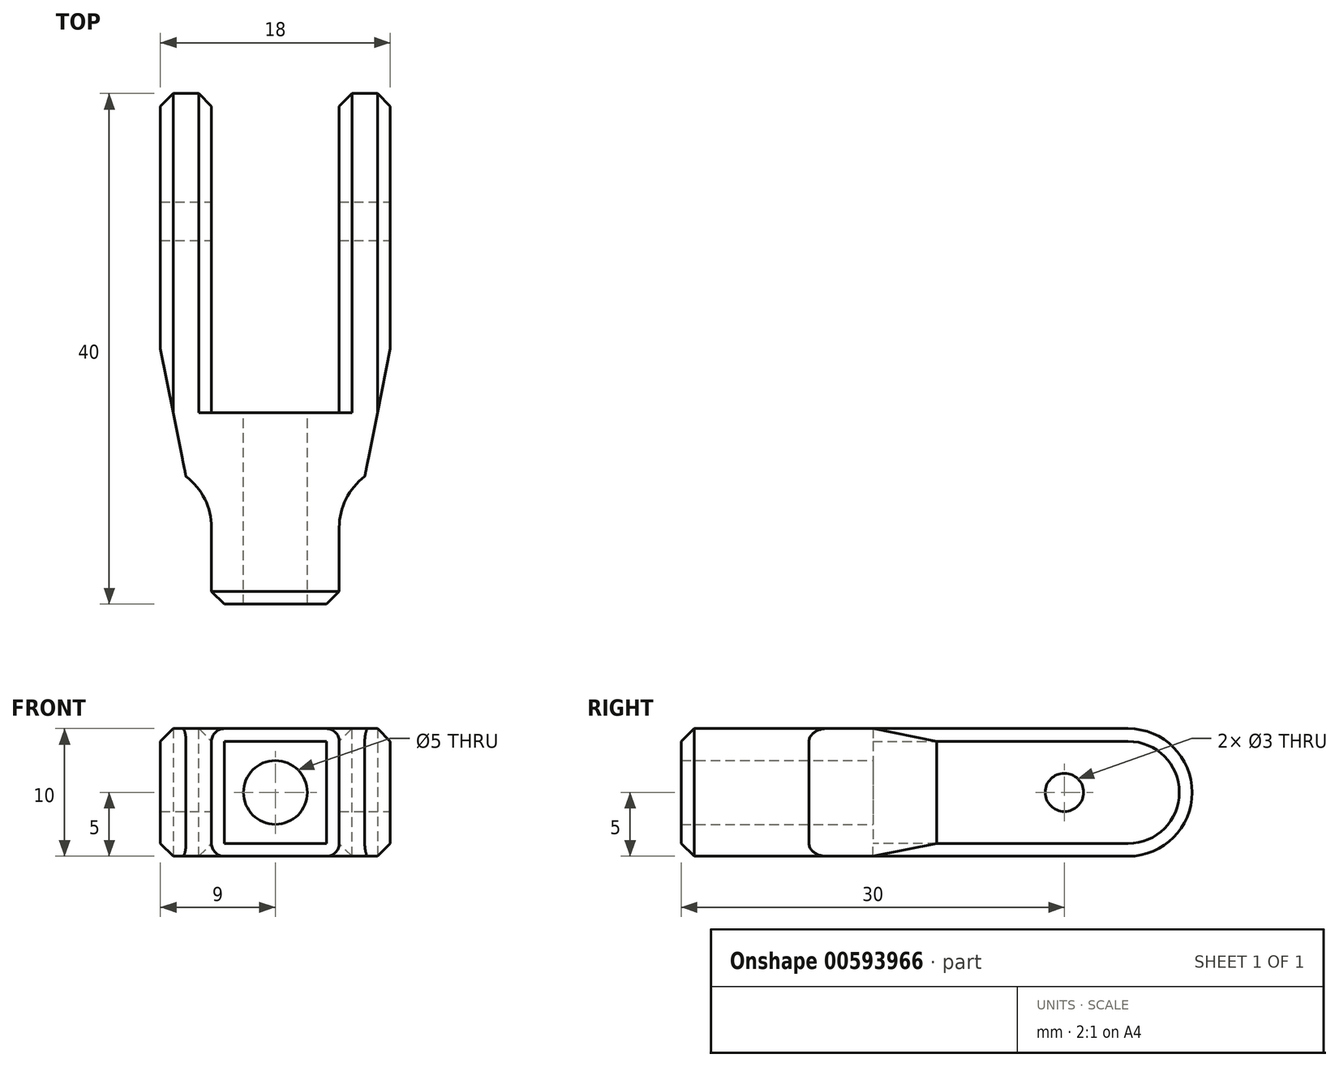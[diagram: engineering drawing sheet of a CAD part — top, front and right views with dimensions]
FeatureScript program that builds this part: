
annotation { "Feature Type Name" : "Feature", "Feature Type Description" : "" }
export const myFeature = defineFeature(function(context is Context, id is Id, definition is map)
    precondition{}
    {
        {
            var Q0;
            Q0=qCreatedBy(makeId("Top.planeOp"),FACE);
            var sketch = newSketch(context, id + "F0", { "sketchPlane" : qUnion([Q0])});
            skLineSegment(sketch, "E0.bottom", {"start": v(-5, 10) * mm, "end": v(5, 10) * mm});
            skLineSegment(sketch, "E0.top", {"start": v(-5, -10) * mm, "end": v(5, -10) * mm});
            skLineSegment(sketch, "E0.left", {"start": v(-5, 10) * mm, "end": v(-5, -10) * mm});
            skLineSegment(sketch, "E0.right", {"start": v(5, 10) * mm, "end": v(5, -10) * mm});
            skPoint(sketch, "E0.middle", {"position": v(0, 0) * mm});
            skLineSegment(sketch, "E1.bottom", {"start": v(-7, 20) * mm, "end": v(7, 20) * mm});
            skLineSegment(sketch, "E1.top", {"start": v(-7, 0) * mm, "end": v(7, 0) * mm});
            skLineSegment(sketch, "E1.left", {"start": v(-7, 20) * mm, "end": v(-7, 0) * mm});
            skLineSegment(sketch, "E1.right", {"start": v(7, 20) * mm, "end": v(7, 0) * mm});
            skPoint(sketch, "E1.middle", {"position": v(0, 10) * mm});
            skLineSegment(sketch, "E2.bottom", {"start": v(-5, 10) * mm, "end": v(-9, 10) * mm});
            skLineSegment(sketch, "E2.top", {"start": v(-5, 30) * mm, "end": v(-9, 30) * mm});
            skLineSegment(sketch, "E2.left", {"start": v(-5, 10) * mm, "end": v(-5, 30) * mm});
            skLineSegment(sketch, "E2.right", {"start": v(-9, 10) * mm, "end": v(-9, 30) * mm});
            skPoint(sketch, "E2.middle", {"position": v(-7, 20) * mm});
            skLineSegment(sketch, "E3.bottom", {"start": v(5, 10) * mm, "end": v(9, 10) * mm});
            skLineSegment(sketch, "E3.top", {"start": v(5, 30) * mm, "end": v(9, 30) * mm});
            skLineSegment(sketch, "E3.left", {"start": v(5, 10) * mm, "end": v(5, 30) * mm});
            skLineSegment(sketch, "E3.right", {"start": v(9, 10) * mm, "end": v(9, 30) * mm});
            skPoint(sketch, "E3.middle", {"position": v(7, 20) * mm});
            skLineSegment(sketch, "E4", {"start": v(-9, 10) * mm, "end": v(-7, 0) * mm});
            skLineSegment(sketch, "E5", {"start": v(7, 0) * mm, "end": v(9, 10) * mm});
            skCircle(sketch, "E6", {"center": v(0, 10) * mm, "radius": 5 * mm});
            skPoint(sketch, "E7", {"position": v(0, 5) * mm});
            skLineSegment(sketch, "E8", {"start": v(-5, 5) * mm, "end": v(5, 5) * mm});
            skSolve(sketch);
        }
        {
            var Q0;
            {var subQ0=sQuery(id+"F0.wireOp",EDGE,"E0.top");Q0=makeQuery(id+"F0.imprint","IMPRINT",FACE,{"disambiguationData":[TD([[makeQuery(id+"F0.imprint","IMPRINT",EDGE,{"derivedFrom":subQ0}),1.0]])]});}
            var Q1;
            {var subQ1=sQuery(id+"F0.wireOp",EDGE,"E0.right");var subQ3=sQuery(id+"F0.wireOp",EDGE,"E1.top");var subQ4=makeQuery(id+"F0.imprint","INTERSECT",VERTEX,{"derivedFrom":[subQ1,subQ3]});Q1=makeQuery(id+"F0.imprint","IMPRINT",FACE,{"disambiguationData":[TD([[makeQuery(id+"F0.imprint","IMPRINT",EDGE,{"disambiguationData":[TD([[subQ4,-1.0]])],"derivedFrom":subQ3}),1.0]])]});}
            var Q2;
            {var subQ0=sQuery(id+"F0.wireOp",EDGE,"E5");Q2=makeQuery(id+"F0.imprint","IMPRINT",FACE,{"disambiguationData":[TD([[makeQuery(id+"F0.imprint","IMPRINT",EDGE,{"derivedFrom":subQ0}),1.0]])]});}
            var Q3;
            {var subQ0=sQuery(id+"F0.wireOp",EDGE,"E3.top");Q3=makeQuery(id+"F0.imprint","IMPRINT",FACE,{"disambiguationData":[TD([[makeQuery(id+"F0.imprint","IMPRINT",EDGE,{"derivedFrom":subQ0}),-1.0]])]});}
            var Q4;
            {var subQ1=sQuery(id+"F0.wireOp",EDGE,"E0.left");var subQ3=sQuery(id+"F0.wireOp",EDGE,"E1.top");var subQ4=makeQuery(id+"F0.imprint","INTERSECT",VERTEX,{"derivedFrom":[subQ1,subQ3]});Q4=makeQuery(id+"F0.imprint","IMPRINT",FACE,{"disambiguationData":[TD([[makeQuery(id+"F0.imprint","IMPRINT",EDGE,{"disambiguationData":[TD([[subQ4,1.0]])],"derivedFrom":subQ3}),1.0]])]});}
            var Q5;
            {var subQ0=sQuery(id+"F0.wireOp",EDGE,"E4");Q5=makeQuery(id+"F0.imprint","IMPRINT",FACE,{"disambiguationData":[TD([[makeQuery(id+"F0.imprint","IMPRINT",EDGE,{"derivedFrom":subQ0}),1.0]])]});}
            var Q6;
            {var subQ0=sQuery(id+"F0.wireOp",EDGE,"E1.left");var subQ1=sQuery(id+"F0.wireOp",EDGE,"E1.bottom");var subQ2=makeQuery(id+"F0.imprint","INTERSECT",VERTEX,{"derivedFrom":[subQ1,subQ0]});Q6=makeQuery(id+"F0.imprint","IMPRINT",FACE,{"disambiguationData":[TD([[makeQuery(id+"F0.imprint","IMPRINT",EDGE,{"disambiguationData":[TD([[subQ2,-1.0]])],"derivedFrom":subQ1}),-1.0]])]});}
            var Q7;
            {var subQ0=sQuery(id+"F0.wireOp",EDGE,"E1.right");var subQ1=sQuery(id+"F0.wireOp",EDGE,"E1.bottom");var subQ2=makeQuery(id+"F0.imprint","INTERSECT",VERTEX,{"derivedFrom":[subQ1,subQ0]});Q7=makeQuery(id+"F0.imprint","IMPRINT",FACE,{"disambiguationData":[TD([[makeQuery(id+"F0.imprint","IMPRINT",EDGE,{"disambiguationData":[TD([[subQ2,1.0]])],"derivedFrom":subQ1}),-1.0]])]});}
            var Q8;
            {var subQ0=sQuery(id+"F0.wireOp",EDGE,"E2.top");Q8=makeQuery(id+"F0.imprint","IMPRINT",FACE,{"disambiguationData":[TD([[makeQuery(id+"F0.imprint","IMPRINT",EDGE,{"derivedFrom":subQ0}),1.0]])]});}
            var Q9;
            {var subQ1=sQuery(id+"F0.wireOp",EDGE,"E0.left");var subQ4=sQuery(id+"F0.wireOp",EDGE,"E1.top");var subQ5=makeQuery(id+"F0.imprint","INTERSECT",VERTEX,{"derivedFrom":[subQ1,subQ4]});Q9=makeQuery(id+"F0.imprint","IMPRINT",FACE,{"disambiguationData":[TD([[makeQuery(id+"F0.imprint","IMPRINT",EDGE,{"disambiguationData":[TD([[subQ5,-1.0]])],"derivedFrom":subQ4}),1.0]])]});}
            extrude(context, id + "F1", {"entities" : qUnion([Q0, Q1, Q2, Q3, Q4, Q5, Q6, Q7, Q8, Q9]), "depth" : 10 * mm, "offsetDistance" : 25 * mm});
        }
        {
            var Q0;
            Q0=makeQuery(id+"F1.opExtrude","SWEPT_FACE",FACE,{"disambiguationData":[OSD([sQuery(id+"F0.wireOp",EDGE,"E3.right")])]});
            var sketch = newSketch(context, id + "F2", { "sketchPlane" : qUnion([Q0])});
            skLineSegment(sketch, "E9", {"start": v(30, 10) * mm, "end": v(10, 0) * mm});
            skLineSegment(sketch, "E10", {"start": v(10, 10) * mm, "end": v(30, 0) * mm});
            skPoint(sketch, "E11", {"position": v(20, 5) * mm});
            skSolve(sketch);
        }
        {
            var Q0;
            Q0=sQuery(id+"F2.wireOp",VERTEX,"E11");
            var Q1;
            Q1=makeQuery(id+"F1.opExtrude","SWEPT_BODY",BODY,{"disambiguationData":[OSD([sQuery(id+"F0.wireOp",EDGE,"E0.top"),sQuery(id+"F0.wireOp",EDGE,"E0.left"),sQuery(id+"F0.wireOp",EDGE,"E0.right"),sQuery(id+"F0.wireOp",EDGE,"E1.top"),sQuery(id+"F0.wireOp",EDGE,"E2.top"),sQuery(id+"F0.wireOp",EDGE,"E2.left"),sQuery(id+"F0.wireOp",EDGE,"E2.right"),sQuery(id+"F0.wireOp",EDGE,"E3.top"),sQuery(id+"F0.wireOp",EDGE,"E3.left"),sQuery(id+"F0.wireOp",EDGE,"E3.right"),sQuery(id+"F0.wireOp",EDGE,"E4"),sQuery(id+"F0.wireOp",EDGE,"E5"),sQuery(id+"F0.wireOp",EDGE,"E6")])]});
            hole(context, id + "F3", {"style" : HoleStyle.SIMPLE, "endStyle" : HoleEndStyle.BLIND, "holeDiameter" : 3 * mm, "majorDiameter" : 5 * mm, "holeDepth" : 30 * mm, "isTappedThrough" : true, "tappedDepth" : 12 * mm, "tapClearance" : 3, "locations" : qUnion([Q0]), "scope" : qUnion([Q1])});
        }
        {
            var Q0;
            Q0=makeQuery(id+"F1.opExtrude","SWEPT_FACE",FACE,{"disambiguationData":[OSD([sQuery(id+"F0.wireOp",EDGE,"E8")])]});
            var sketch = newSketch(context, id + "F4", { "sketchPlane" : qUnion([Q0])});
            skLineSegment(sketch, "E12", {"start": v(5, 0) * mm, "end": v(-5, 10) * mm});
            skLineSegment(sketch, "E13", {"start": v(5, 10) * mm, "end": v(-5, 0) * mm});
            skPoint(sketch, "E14", {"position": v(0, 5) * mm});
            skSolve(sketch);
        }
        {
            var Q0;
            Q0=sQuery(id+"F4.wireOp",VERTEX,"E14");
            var Q1;
            Q1=makeQuery(id+"F1.opExtrude","SWEPT_BODY",BODY,{"disambiguationData":[OSD([sQuery(id+"F0.wireOp",EDGE,"E0.top"),sQuery(id+"F0.wireOp",EDGE,"E0.left"),sQuery(id+"F0.wireOp",EDGE,"E0.right"),sQuery(id+"F0.wireOp",EDGE,"E1.top"),sQuery(id+"F0.wireOp",EDGE,"E2.top"),sQuery(id+"F0.wireOp",EDGE,"E2.left"),sQuery(id+"F0.wireOp",EDGE,"E2.right"),sQuery(id+"F0.wireOp",EDGE,"E3.top"),sQuery(id+"F0.wireOp",EDGE,"E3.left"),sQuery(id+"F0.wireOp",EDGE,"E3.right"),sQuery(id+"F0.wireOp",EDGE,"E4"),sQuery(id+"F0.wireOp",EDGE,"E5"),sQuery(id+"F0.wireOp",EDGE,"E8")])]});
            hole(context, id + "F5", {"style" : HoleStyle.SIMPLE, "endStyle" : HoleEndStyle.BLIND, "holeDiameter" : 5 * mm, "majorDiameter" : 5 * mm, "holeDepth" : 30 * mm, "isTappedThrough" : true, "tappedDepth" : 12 * mm, "tapClearance" : 3, "locations" : qUnion([Q0]), "scope" : qUnion([Q1])});
        }
        {
            var Q0;
            Q0=makeQuery(id+"F1.opExtrude","SWEPT_EDGE",EDGE,{"disambiguationData":[OSD([sQuery(id+"F0.wireOp",EDGE,"E0.right"),sQuery(id+"F0.wireOp",EDGE,"E1.top")])]});
            var Q1;
            Q1=makeQuery(id+"F1.opExtrude","SWEPT_EDGE",EDGE,{"disambiguationData":[OSD([sQuery(id+"F0.wireOp",EDGE,"E0.left"),sQuery(id+"F0.wireOp",EDGE,"E1.top")])]});
            fillet(context, id + "F6", {"entities" : qUnion([Q0, Q1]), "radius" : 5 * mm, "tangentPropagation" : true, "allowEdgeOverflow" : false});
        }
        {
            var Q0;
            {var subQ0=sQuery(id+"F0.wireOp",EDGE,"E1.top");var subQ1=sQuery(id+"F0.wireOp",EDGE,"E0.right");Q0=makeQuery(id+"F6.opFillet","BLEND_EDGE",EDGE,{"blendedFrom":[makeQuery(id+"F1.opExtrude","SWEPT_EDGE",EDGE,{"disambiguationData":[OSD([subQ1,subQ0])]}),makeQuery(id+"F1.opExtrude","CAP_FACE",FACE,{"disambiguationData":[OSD([sQuery(id+"F0.wireOp",EDGE,"E0.top"),sQuery(id+"F0.wireOp",EDGE,"E0.left"),subQ1,subQ0,sQuery(id+"F0.wireOp",EDGE,"E2.top"),sQuery(id+"F0.wireOp",EDGE,"E2.left"),sQuery(id+"F0.wireOp",EDGE,"E2.right"),sQuery(id+"F0.wireOp",EDGE,"E3.top"),sQuery(id+"F0.wireOp",EDGE,"E3.left"),sQuery(id+"F0.wireOp",EDGE,"E3.right"),sQuery(id+"F0.wireOp",EDGE,"E4"),sQuery(id+"F0.wireOp",EDGE,"E5"),sQuery(id+"F0.wireOp",EDGE,"E8")])],"isStart":false})],"blendedInto":[makeQuery(id+"F1.opExtrude","CAP_FACE",FACE,{"disambiguationData":[OSD([sQuery(id+"F0.wireOp",EDGE,"E0.top"),sQuery(id+"F0.wireOp",EDGE,"E0.left"),subQ1,subQ0,sQuery(id+"F0.wireOp",EDGE,"E2.top"),sQuery(id+"F0.wireOp",EDGE,"E2.left"),sQuery(id+"F0.wireOp",EDGE,"E2.right"),sQuery(id+"F0.wireOp",EDGE,"E3.top"),sQuery(id+"F0.wireOp",EDGE,"E3.left"),sQuery(id+"F0.wireOp",EDGE,"E3.right"),sQuery(id+"F0.wireOp",EDGE,"E4"),sQuery(id+"F0.wireOp",EDGE,"E5"),sQuery(id+"F0.wireOp",EDGE,"E8")])],"isStart":false})]});}
            var Q1;
            {var subQ0=sQuery(id+"F0.wireOp",EDGE,"E1.top");var subQ1=sQuery(id+"F0.wireOp",EDGE,"E0.left");Q1=makeQuery(id+"F6.opFillet","BLEND_EDGE",EDGE,{"blendedFrom":[makeQuery(id+"F1.opExtrude","SWEPT_EDGE",EDGE,{"disambiguationData":[OSD([subQ1,subQ0])]}),makeQuery(id+"F1.opExtrude","CAP_FACE",FACE,{"disambiguationData":[OSD([sQuery(id+"F0.wireOp",EDGE,"E0.top"),subQ1,sQuery(id+"F0.wireOp",EDGE,"E0.right"),subQ0,sQuery(id+"F0.wireOp",EDGE,"E2.top"),sQuery(id+"F0.wireOp",EDGE,"E2.left"),sQuery(id+"F0.wireOp",EDGE,"E2.right"),sQuery(id+"F0.wireOp",EDGE,"E3.top"),sQuery(id+"F0.wireOp",EDGE,"E3.left"),sQuery(id+"F0.wireOp",EDGE,"E3.right"),sQuery(id+"F0.wireOp",EDGE,"E4"),sQuery(id+"F0.wireOp",EDGE,"E5"),sQuery(id+"F0.wireOp",EDGE,"E8")])],"isStart":false})],"blendedInto":[makeQuery(id+"F1.opExtrude","CAP_FACE",FACE,{"disambiguationData":[OSD([sQuery(id+"F0.wireOp",EDGE,"E0.top"),subQ1,sQuery(id+"F0.wireOp",EDGE,"E0.right"),subQ0,sQuery(id+"F0.wireOp",EDGE,"E2.top"),sQuery(id+"F0.wireOp",EDGE,"E2.left"),sQuery(id+"F0.wireOp",EDGE,"E2.right"),sQuery(id+"F0.wireOp",EDGE,"E3.top"),sQuery(id+"F0.wireOp",EDGE,"E3.left"),sQuery(id+"F0.wireOp",EDGE,"E3.right"),sQuery(id+"F0.wireOp",EDGE,"E4"),sQuery(id+"F0.wireOp",EDGE,"E5"),sQuery(id+"F0.wireOp",EDGE,"E8")])],"isStart":false})]});}
            var Q2;
            {var subQ0=sQuery(id+"F0.wireOp",EDGE,"E1.top");var subQ1=sQuery(id+"F0.wireOp",EDGE,"E0.left");Q2=makeQuery(id+"F6.opFillet","BLEND_EDGE",EDGE,{"blendedFrom":[makeQuery(id+"F1.opExtrude","SWEPT_EDGE",EDGE,{"disambiguationData":[OSD([subQ1,subQ0])]}),makeQuery(id+"F1.opExtrude","CAP_FACE",FACE,{"disambiguationData":[OSD([sQuery(id+"F0.wireOp",EDGE,"E0.top"),subQ1,sQuery(id+"F0.wireOp",EDGE,"E0.right"),subQ0,sQuery(id+"F0.wireOp",EDGE,"E2.top"),sQuery(id+"F0.wireOp",EDGE,"E2.left"),sQuery(id+"F0.wireOp",EDGE,"E2.right"),sQuery(id+"F0.wireOp",EDGE,"E3.top"),sQuery(id+"F0.wireOp",EDGE,"E3.left"),sQuery(id+"F0.wireOp",EDGE,"E3.right"),sQuery(id+"F0.wireOp",EDGE,"E4"),sQuery(id+"F0.wireOp",EDGE,"E5"),sQuery(id+"F0.wireOp",EDGE,"E8")])],"isStart":true})],"blendedInto":[makeQuery(id+"F1.opExtrude","CAP_FACE",FACE,{"disambiguationData":[OSD([sQuery(id+"F0.wireOp",EDGE,"E0.top"),subQ1,sQuery(id+"F0.wireOp",EDGE,"E0.right"),subQ0,sQuery(id+"F0.wireOp",EDGE,"E2.top"),sQuery(id+"F0.wireOp",EDGE,"E2.left"),sQuery(id+"F0.wireOp",EDGE,"E2.right"),sQuery(id+"F0.wireOp",EDGE,"E3.top"),sQuery(id+"F0.wireOp",EDGE,"E3.left"),sQuery(id+"F0.wireOp",EDGE,"E3.right"),sQuery(id+"F0.wireOp",EDGE,"E4"),sQuery(id+"F0.wireOp",EDGE,"E5"),sQuery(id+"F0.wireOp",EDGE,"E8")])],"isStart":true})]});}
            var Q3;
            {var subQ0=sQuery(id+"F0.wireOp",EDGE,"E1.top");var subQ1=sQuery(id+"F0.wireOp",EDGE,"E0.right");Q3=makeQuery(id+"F6.opFillet","BLEND_EDGE",EDGE,{"blendedFrom":[makeQuery(id+"F1.opExtrude","SWEPT_EDGE",EDGE,{"disambiguationData":[OSD([subQ1,subQ0])]}),makeQuery(id+"F1.opExtrude","CAP_FACE",FACE,{"disambiguationData":[OSD([sQuery(id+"F0.wireOp",EDGE,"E0.top"),sQuery(id+"F0.wireOp",EDGE,"E0.left"),subQ1,subQ0,sQuery(id+"F0.wireOp",EDGE,"E2.top"),sQuery(id+"F0.wireOp",EDGE,"E2.left"),sQuery(id+"F0.wireOp",EDGE,"E2.right"),sQuery(id+"F0.wireOp",EDGE,"E3.top"),sQuery(id+"F0.wireOp",EDGE,"E3.left"),sQuery(id+"F0.wireOp",EDGE,"E3.right"),sQuery(id+"F0.wireOp",EDGE,"E4"),sQuery(id+"F0.wireOp",EDGE,"E5"),sQuery(id+"F0.wireOp",EDGE,"E8")])],"isStart":true})],"blendedInto":[makeQuery(id+"F1.opExtrude","CAP_FACE",FACE,{"disambiguationData":[OSD([sQuery(id+"F0.wireOp",EDGE,"E0.top"),sQuery(id+"F0.wireOp",EDGE,"E0.left"),subQ1,subQ0,sQuery(id+"F0.wireOp",EDGE,"E2.top"),sQuery(id+"F0.wireOp",EDGE,"E2.left"),sQuery(id+"F0.wireOp",EDGE,"E2.right"),sQuery(id+"F0.wireOp",EDGE,"E3.top"),sQuery(id+"F0.wireOp",EDGE,"E3.left"),sQuery(id+"F0.wireOp",EDGE,"E3.right"),sQuery(id+"F0.wireOp",EDGE,"E4"),sQuery(id+"F0.wireOp",EDGE,"E5"),sQuery(id+"F0.wireOp",EDGE,"E8")])],"isStart":true})]});}
            fillet(context, id + "F7", {"entities" : qUnion([Q0, Q1, Q2, Q3]), "radius" : 1 * mm, "tangentPropagation" : true, "allowEdgeOverflow" : false});
        }
        {
            var Q0;
            Q0=makeQuery(id+"F1.opExtrude","CAP_EDGE",EDGE,{"disambiguationData":[OSD([sQuery(id+"F0.wireOp",EDGE,"E2.top")])],"isStart":false});
            var Q1;
            Q1=makeQuery(id+"F1.opExtrude","CAP_EDGE",EDGE,{"disambiguationData":[OSD([sQuery(id+"F0.wireOp",EDGE,"E2.top")])],"isStart":true});
            var Q2;
            Q2=makeQuery(id+"F1.opExtrude","CAP_EDGE",EDGE,{"disambiguationData":[OSD([sQuery(id+"F0.wireOp",EDGE,"E3.top")])],"isStart":true});
            var Q3;
            Q3=makeQuery(id+"F1.opExtrude","CAP_EDGE",EDGE,{"disambiguationData":[OSD([sQuery(id+"F0.wireOp",EDGE,"E3.top")])],"isStart":false});
            fillet(context, id + "F8", {"entities" : qUnion([Q0, Q1, Q2, Q3]), "radius" : 5 * mm, "tangentPropagation" : true, "allowEdgeOverflow" : false});
        }
        {
            var Q0;
            Q0=makeQuery(id+"F1.opExtrude","CAP_EDGE",EDGE,{"disambiguationData":[OSD([sQuery(id+"F0.wireOp",EDGE,"E0.left"),sQuery(id+"F0.wireOp",EDGE,"E2.left")])],"isStart":false});
            var Q1;
            Q1=makeQuery(id+"F1.opExtrude","CAP_EDGE",EDGE,{"disambiguationData":[OSD([sQuery(id+"F0.wireOp",EDGE,"E0.right"),sQuery(id+"F0.wireOp",EDGE,"E3.left")])],"isStart":false});
            var Q2;
            Q2=makeQuery(id+"F1.opExtrude","CAP_EDGE",EDGE,{"disambiguationData":[OSD([sQuery(id+"F0.wireOp",EDGE,"E3.right")])],"isStart":false});
            var Q3;
            Q3=makeQuery(id+"F1.opExtrude","CAP_EDGE",EDGE,{"disambiguationData":[OSD([sQuery(id+"F0.wireOp",EDGE,"E2.right")])],"isStart":false});
            chamfer(context, id + "F9", {"entities" : qUnion([Q0, Q1, Q2, Q3]), "width" : 1 * mm, "tangentPropagation" : true});
        }
        {
            var Q0;
            Q0=makeQuery(id+"F5.hole-0.boolean.opBoolean","COPY",EDGE,{"derivedFrom":makeQuery(id+"F5.hole-0.opRevolve","SWEPT_EDGE",EDGE,{"disambiguationData":[OSD([sQuery(id+"F5.hole-0.sketch.wireOp",EDGE,"core_line_2"),sQuery(id+"F5.hole-0.sketch.wireOp",EDGE,"core_line_3")])]})});
            var Q1;
            Q1=makeQuery(id+"F5.hole-0.boolean.opBoolean","INTERSECT",EDGE,{"derivedFrom":[makeQuery(id+"F1.opExtrude","SWEPT_FACE",FACE,{"disambiguationData":[OSD([sQuery(id+"F0.wireOp",EDGE,"E0.top")])]}),makeQuery(id+"F5.hole-0.opRevolve","SWEPT_FACE",FACE,{"disambiguationData":[OSD([sQuery(id+"F5.hole-0.sketch.wireOp",EDGE,"core_line_2")])]})]});
            var Q2;
            Q2=makeQuery(id+"F1.opExtrude","CAP_EDGE",EDGE,{"disambiguationData":[OSD([sQuery(id+"F0.wireOp",EDGE,"E0.top")])],"isStart":false});
            chamfer(context, id + "F10", {"entities" : qUnion([Q0, Q1, Q2]), "width" : 1 * mm, "tangentPropagation" : true});
        }
    });
